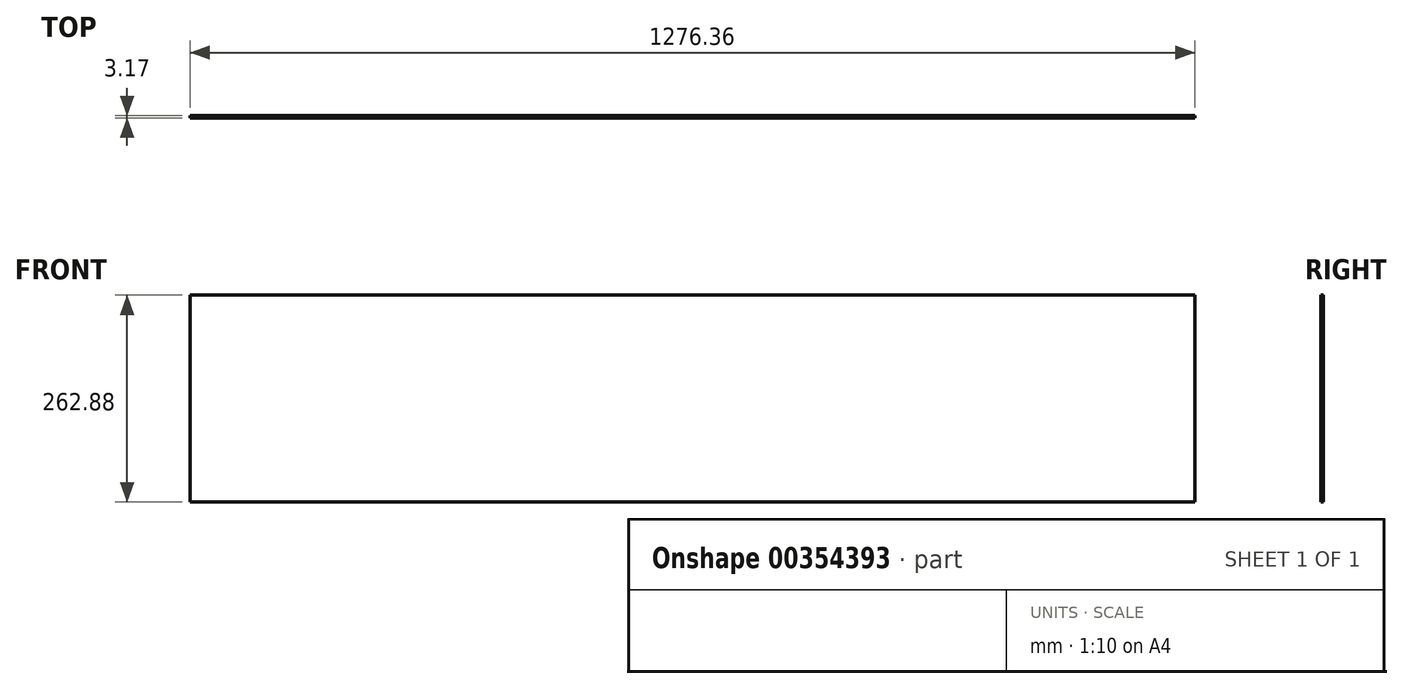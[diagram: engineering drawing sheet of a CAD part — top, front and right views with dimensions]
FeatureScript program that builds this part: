
annotation { "Feature Type Name" : "Feature", "Feature Type Description" : "" }
export const myFeature = defineFeature(function(context is Context, id is Id, definition is map)
    precondition{}
    {
        {
            var Q0;
            Q0=qCreatedBy(makeId("Front.planeOp"),FACE);
            var sketch = newSketch(context, id + "F0", { "sketchPlane" : qUnion([Q0])});
            skLineSegment(sketch, "E0.bottom", {"start": v(638.17, 131.44) * mm, "end": v(-638.17, 131.45) * mm});
            skLineSegment(sketch, "E0.top", {"start": v(638.18, -131.44) * mm, "end": v(-638.17, -131.44) * mm});
            skLineSegment(sketch, "E0.left", {"start": v(638.18, 131.44) * mm, "end": v(638.18, -131.45) * mm});
            skLineSegment(sketch, "E0.right", {"start": v(-638.17, 131.45) * mm, "end": v(-638.18, -131.45) * mm});
            skPoint(sketch, "E0.middle", {"position": v(0, 0) * mm});
            skSolve(sketch);
        }
        {
            var Q0;
            Q0 = qSketchRegion(id + "F0", true);
            extrude(context, id + "F1", {"entities" : qUnion([Q0]), "depth" : 3.17 * mm});
        }
    });
